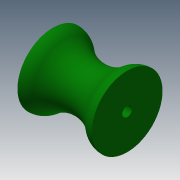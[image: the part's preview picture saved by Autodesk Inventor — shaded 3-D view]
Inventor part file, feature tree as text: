
AUTODESK INVENTOR PART (.ipt)
format: ipt  version: 2013 (Build 170138000, 138)  size: 201,216 bytes
history: native  units: mm
features: sketch x2, revolve x1, extrude x1, fillet x1
ambient origin geometry x8: Origin, YZ Plane, XZ Plane, XY Plane, X Axis, Y Axis, Z Axis, Center Point
bodies: Solid1 (feature_tree)
feature tree (5):
  revolve  "Revolution1"  [1 undecoded]
  extrude  "Extrusion1"  Depth=7.0mm
  fillet  "Fillet2"  Radius=52.7mm
  sketch  "Sketch1"  dims[d2=5.0mm d4=5.0mm]
  sketch  "Sketch2"  dims[d7=90.0deg d8=7.0mm d9=52.7mm d10=0.0mm d12=12.0mm]
note: 1 required parameter value undecoded (feature->parameter linkage not recoverable at this tier; creation-order binding heuristic only, values carry confidence <= 0.55)
